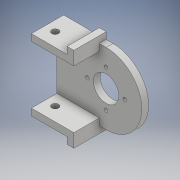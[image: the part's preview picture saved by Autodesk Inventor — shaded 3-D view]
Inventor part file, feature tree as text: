
AUTODESK INVENTOR PART (.ipt)
format: ipt  version: 2018 (Build 220112000, 112)  size: 171,520 bytes
history: native  units: mm
features: extrude x4, sketch x4, hole x3, fillet x1, pattern_circular x1
ambient origin geometry x8: Origin, YZ Plane, XZ Plane, XY Plane, X Axis, Y Axis, Z Axis, Center Point
bodies: Solid1 (feature_tree)
feature tree (13):
  extrude  "Extrusion1"  Depth=4.0mm
  extrude  "Extrusion2"  Depth=42.0mm
  fillet  "Fillet1"  Radius=50.0mm
  hole  "Hole1"  [1 undecoded]
  hole  "Hole2"  [1 undecoded]
  hole  "Hole6"  [1 undecoded]
  pattern_circular  "Circular Pattern1"  Count=4 Angle=360.0deg
  extrude  "Extrusion3"  Depth=4.0mm
  extrude  "Extrusion4"  Depth=4.0mm TaperAngle=0.0deg
  sketch  "Sketch1"  dims[d0=4.0mm d1=4.0mm]
  sketch  "Sketch2"  dims[d2=15.0mm d3=42.0mm d4=50.0mm d5=0.0mm]
  sketch  "Sketch3"  dims[d6=15.0mm d7=25.0mm]
  sketch  "Sketch4"  dims[d8=50.0mm d9=0.0mm d10=21.0mm d11=10.0mm d12=10.0mm d13=15.0mm d14=6.0mm d15=4.0mm d16=2.0mm d17=90.0deg d18=8.0mm d19=20.594885mm d20=10.0mm d69=29.0mm d22=2.0mm d23=6.0mm d24=4.0mm d25=2.0mm d26=90.0deg d27=8.0mm d28=20.594885mm d56=6.0mm d70=8.0mm d58=4.0mm d59=6.0mm d60=4.0mm d61=2.0mm d62=90.0deg d63=42.0mm d64=0.0mm d65=40.0mm d66=360.0deg d68=4.0mm d71=4.0mm d72=0.0mm d73=4.0mm d74=4.0mm d75=0.0mm]
note: 3 required parameter values undecoded (feature->parameter linkage not recoverable at this tier; creation-order binding heuristic only, values carry confidence <= 0.55)
